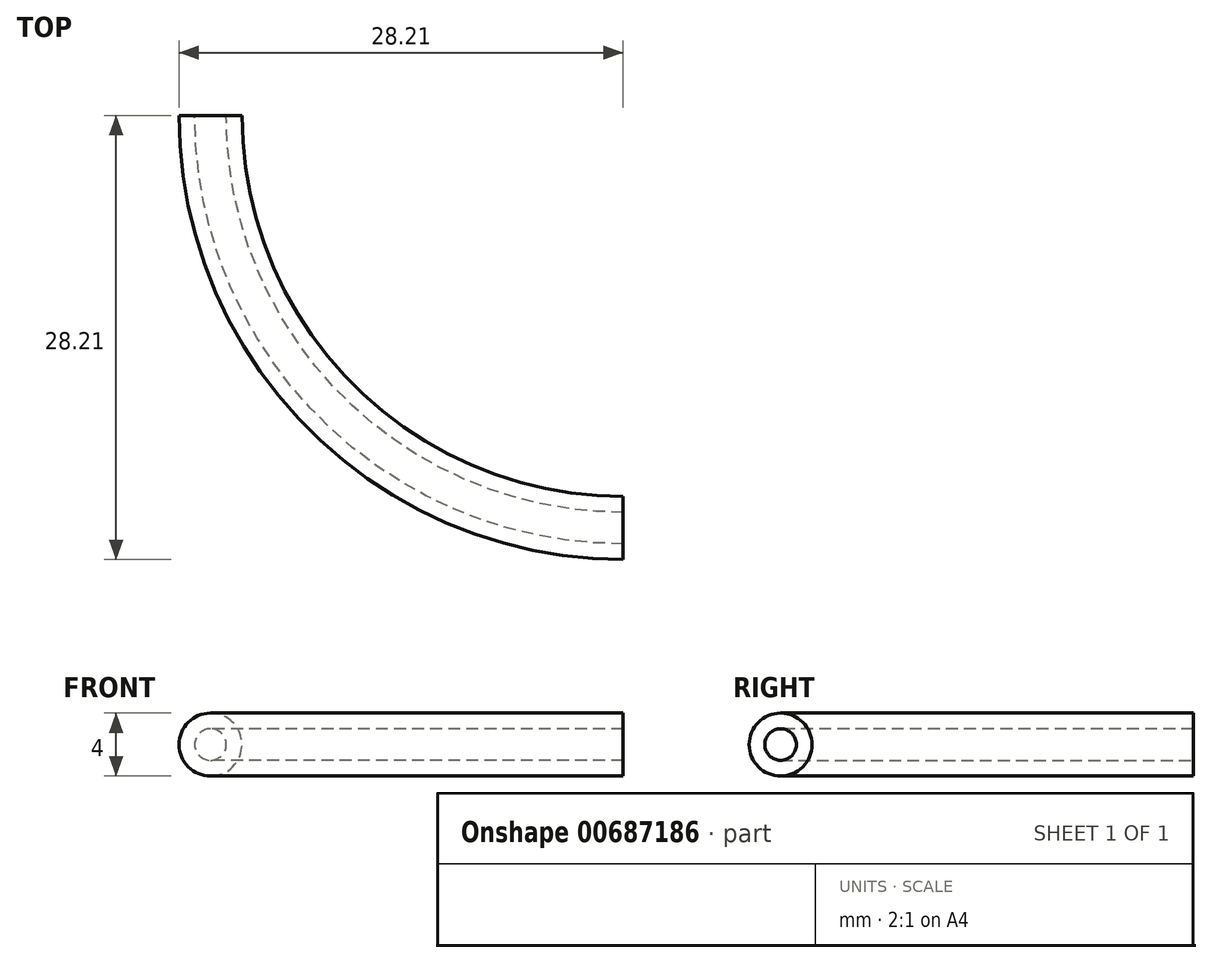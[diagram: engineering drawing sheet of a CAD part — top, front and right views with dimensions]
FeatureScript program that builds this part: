
annotation { "Feature Type Name" : "Feature", "Feature Type Description" : "" }
export const myFeature = defineFeature(function(context is Context, id is Id, definition is map)
    precondition{}
    {
        {
            var Q0;
            Q0=qCreatedBy(makeId("Front.planeOp"),FACE);
            var sketch = newSketch(context, id + "F0", { "sketchPlane" : qUnion([Q0])});
            skCircle(sketch, "E0", {"center": v(-26.2, 0) * mm, "radius": 1 * mm});
            skCircle(sketch, "E1", {"center": v(-26.2, 0) * mm, "radius": 2 * mm});
            skSolve(sketch);
        }
        {
            var Q0;
            Q0=qCreatedBy(makeId("Top.planeOp"),FACE);
            var sketch = newSketch(context, id + "F1", { "sketchPlane" : qUnion([Q0])});
            skCircle(sketch, "E2", {"center": v(0, 0) * mm, "radius": 26.27 * mm});
            skSolve(sketch);
        }
        {
            var Q0;
            Q0 = qSketchRegion(id + "F0", true);
            var Q1;
            Q1=sQuery(id+"F1.wireOp",EDGE,"E2");
            revolve(context, id + "F2", {"entities" : qUnion([Q0]), "axis" : qUnion([Q1]), "revolveType" : RevolveType.ONE_DIRECTION, "angle" : 90 * degree});
        }
    });
